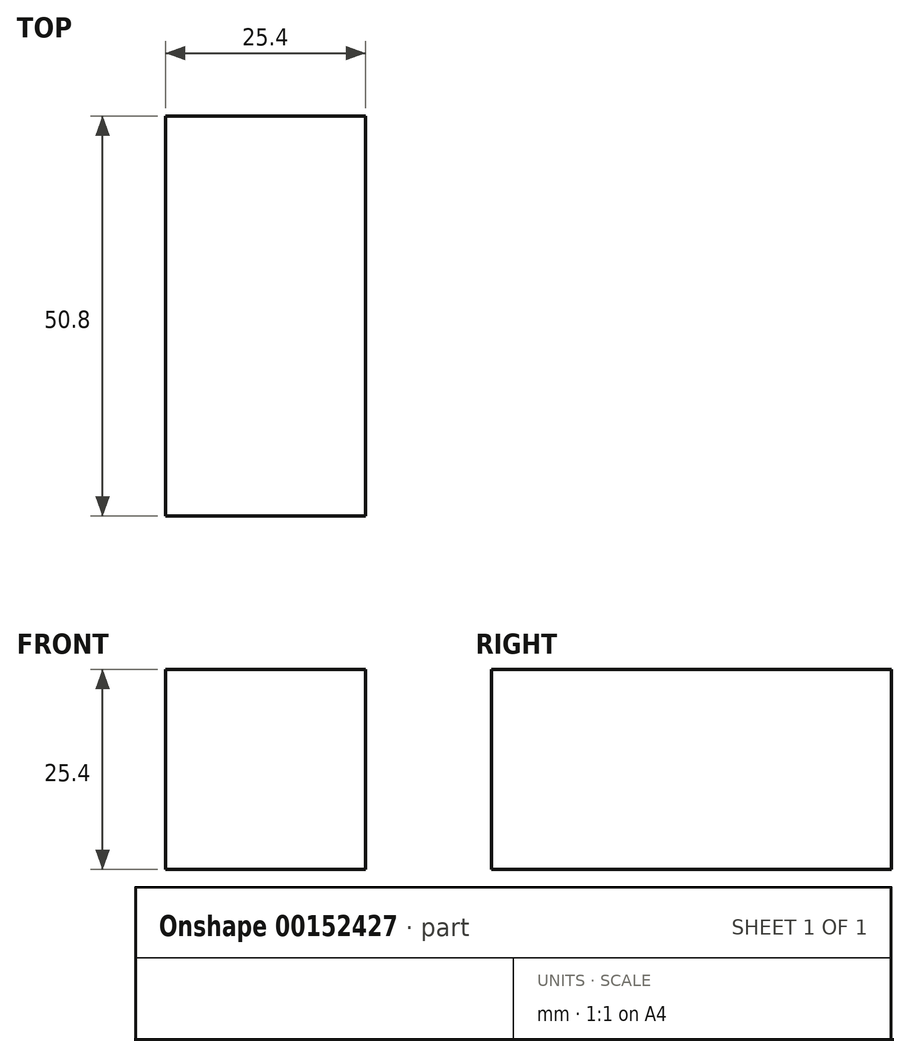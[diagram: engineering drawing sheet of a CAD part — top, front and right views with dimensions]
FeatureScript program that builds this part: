
annotation { "Feature Type Name" : "Feature", "Feature Type Description" : "" }
export const myFeature = defineFeature(function(context is Context, id is Id, definition is map)
    precondition{}
    {
        {
            var Q0;
            Q0=qCreatedBy(makeId("Front.planeOp"),FACE);
            var sketch = newSketch(context, id + "F0", { "sketchPlane" : qUnion([Q0])});
            skLineSegment(sketch, "E0.bottom", {"start": v(-12.7, 11.18) * mm, "end": v(12.7, 11.18) * mm});
            skLineSegment(sketch, "E0.top", {"start": v(-12.7, -14.22) * mm, "end": v(12.7, -14.22) * mm});
            skLineSegment(sketch, "E0.left", {"start": v(-12.7, 11.18) * mm, "end": v(-12.7, -14.22) * mm});
            skLineSegment(sketch, "E0.right", {"start": v(12.7, 11.18) * mm, "end": v(12.7, -14.22) * mm});
            skSolve(sketch);
        }
        {
            var Q0;
            Q0 = qSketchRegion(id + "F0", true);
            var Q1;
            Q1=makeQuery(id+"F0.imprint","IMPRINT",FACE,{"disambiguationData":[TD([[makeQuery(id+"F0.imprint","IMPRINT",EDGE,{"derivedFrom":sQuery(id+"F0.wireOp",EDGE,"E0.bottom")}),-1.0]])]});
            extrude(context, id + "F1", {"entities" : qUnion([Q0, Q1]), "depth" : 50.8 * mm});
        }
    });
